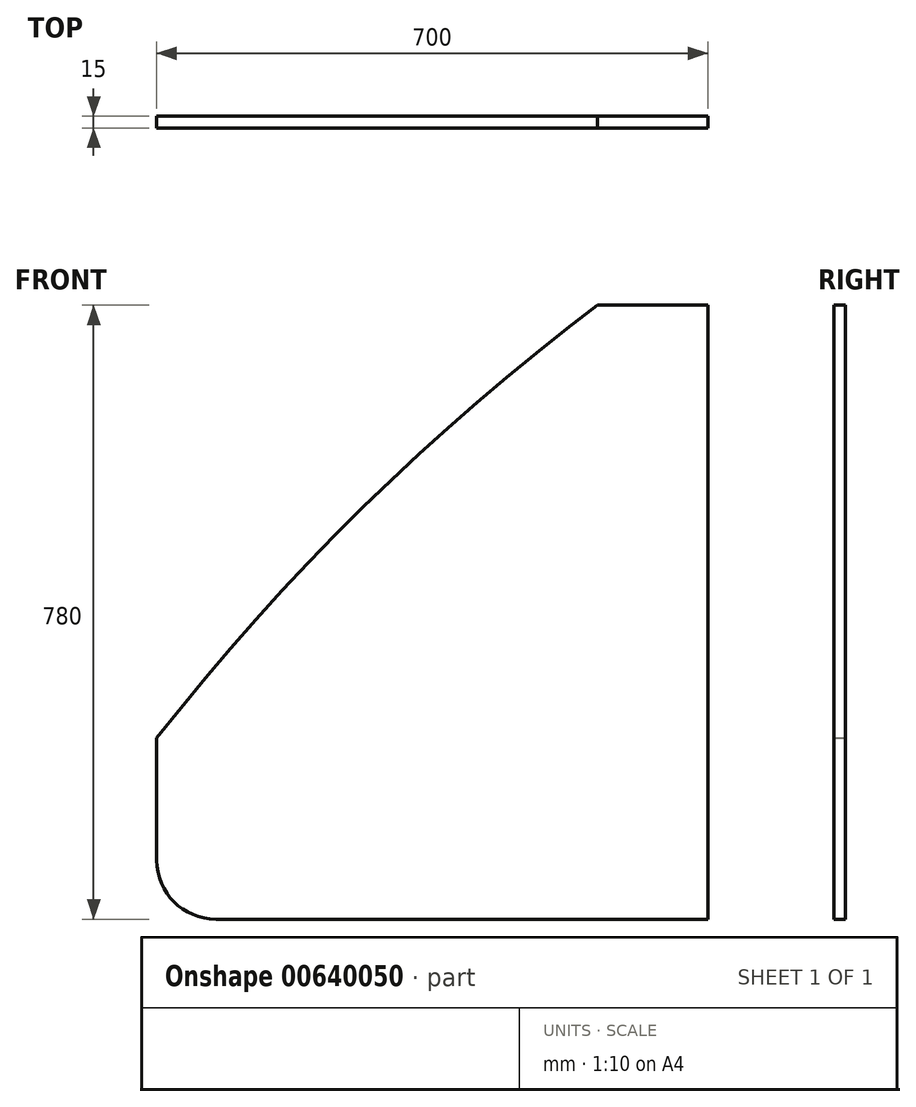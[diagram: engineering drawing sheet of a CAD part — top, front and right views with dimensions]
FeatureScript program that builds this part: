
annotation { "Feature Type Name" : "Feature", "Feature Type Description" : "" }
export const myFeature = defineFeature(function(context is Context, id is Id, definition is map)
    precondition{}
    {
        {
            var Q0;
            Q0=qCreatedBy(makeId("Front.planeOp"),FACE);
            var sketch = newSketch(context, id + "F0", { "sketchPlane" : qUnion([Q0])});
            skLineSegment(sketch, "E0", {"start": v(0, 0) * mm, "end": v(0, 780) * mm});
            skLineSegment(sketch, "E1", {"start": v(0, 0) * mm, "end": v(-700, 0) * mm});
            skLineSegment(sketch, "E2", {"start": v(-700, 0) * mm, "end": v(-700, 230) * mm});
            skLineSegment(sketch, "E3", {"start": v(-140, 780) * mm, "end": v(0, 780) * mm});
            skArc(sketch, "E4", {"start": v(-140, 780) * mm, "mid": v(-438.07, 523.4) * mm, "end": v(-700, 230) * mm});
            skSolve(sketch);
        }
        {
            var Q0;
            Q0=makeQuery(id+"F0.imprint","IMPRINT",FACE,{"disambiguationData":[TD([[makeQuery(id+"F0.imprint","IMPRINT",EDGE,{"derivedFrom":sQuery(id+"F0.wireOp",EDGE,"E0")}),1.0]])]});
            extrude(context, id + "F1", {"entities" : qUnion([Q0]), "depth" : 15 * mm, "offsetDistance" : 25 * mm});
        }
        {
            var Q0;
            Q0=makeQuery(id+"F1.opExtrude","SWEPT_EDGE",EDGE,{"disambiguationData":[OSD([sQuery(id+"F0.wireOp",EDGE,"E1"),sQuery(id+"F0.wireOp",EDGE,"E2")])]});
            fillet(context, id + "F2", {"entities" : qUnion([Q0]), "radius" : 75 * mm, "tangentPropagation" : true, "allowEdgeOverflow" : false});
        }
    });
